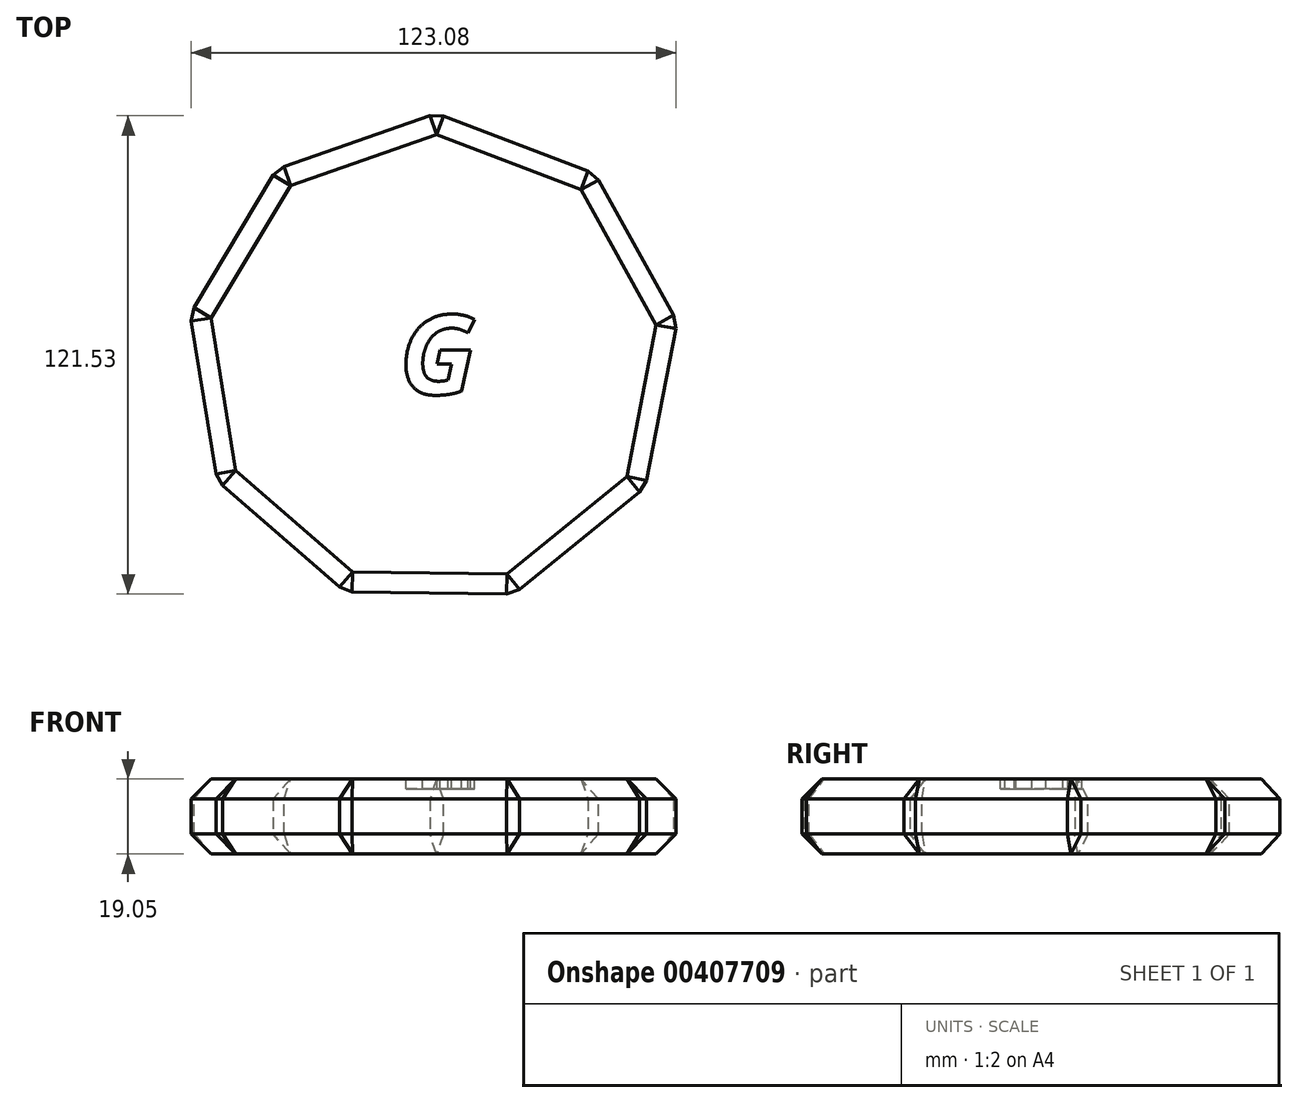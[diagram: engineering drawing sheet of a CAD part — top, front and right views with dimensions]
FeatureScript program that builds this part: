
annotation { "Feature Type Name" : "Feature", "Feature Type Description" : "" }
export const myFeature = defineFeature(function(context is Context, id is Id, definition is map)
    precondition{}
    {
        {
            var Q0;
            Q0=qCreatedBy(makeId("Top.planeOp"),FACE);
            var sketch = newSketch(context, id + "F0", { "sketchPlane" : qUnion([Q0])});
            skCircle(sketch, "E0.cCircle", {"center": v(3.24, 5.3) * mm, "radius": 59.03 * mm, "construction": true});
            skLineSegment(sketch, "E0.0", {"start": v(44.35, 52.8) * mm, "end": v(65.26, 15.27) * mm});
            skLineSegment(sketch, "E0.1", {"start": v(65.26, 15.27) * mm, "end": v(57.16, -26.93) * mm});
            skLineSegment(sketch, "E0.2", {"start": v(57.16, -26.93) * mm, "end": v(23.82, -54.05) * mm});
            skLineSegment(sketch, "E0.3", {"start": v(23.82, -54.05) * mm, "end": v(-19.14, -53.4) * mm});
            skLineSegment(sketch, "E0.4", {"start": v(-19.14, -53.4) * mm, "end": v(-51.63, -25.27) * mm});
            skLineSegment(sketch, "E0.5", {"start": v(-51.63, -25.27) * mm, "end": v(-58.45, 17.16) * mm});
            skLineSegment(sketch, "E0.6", {"start": v(-58.45, 17.16) * mm, "end": v(-36.4, 54.04) * mm});
            skLineSegment(sketch, "E0.7", {"start": v(-36.4, 54.04) * mm, "end": v(4.2, 68.11) * mm});
            skLineSegment(sketch, "E0.8", {"start": v(4.2, 68.11) * mm, "end": v(44.35, 52.8) * mm});
            skPoint(sketch, "E0.0.midPoint", {"position": v(54.8, 34.03) * mm});
            skSolve(sketch);
        }
        {
            var Q0;
            Q0=makeQuery(id+"F0.imprint","IMPRINT",FACE,{"disambiguationData":[TD([[makeQuery(id+"F0.imprint","IMPRINT",EDGE,{"derivedFrom":sQuery(id+"F0.wireOp",EDGE,"E0.0")}),-1.0]])]});
            extrude(context, id + "F1", {"entities" : qUnion([Q0]), "depth" : 19.05 * mm});
        }
        {
            var Q0;
            Q0=makeQuery(id+"F1.opExtrude","CAP_FACE",FACE,{"disambiguationData":[OSD([sQuery(id+"F0.wireOp",EDGE,"E0.0"),sQuery(id+"F0.wireOp",EDGE,"E0.1"),sQuery(id+"F0.wireOp",EDGE,"E0.2"),sQuery(id+"F0.wireOp",EDGE,"E0.3"),sQuery(id+"F0.wireOp",EDGE,"E0.4"),sQuery(id+"F0.wireOp",EDGE,"E0.5"),sQuery(id+"F0.wireOp",EDGE,"E0.6"),sQuery(id+"F0.wireOp",EDGE,"E0.7"),sQuery(id+"F0.wireOp",EDGE,"E0.8")])],"isStart":false});
            var sketch = newSketch(context, id + "F2", { "sketchPlane" : qUnion([Q0])});
            skText(sketch, "E1", { "text": "G", "fontName": "OpenSans-BoldItalic.ttf"});
            const initialGuessF2  = {"E1": [-0.00532, -0.00325, 1, 0, 0.02026]};
            skSetInitialGuess(sketch, initialGuessF2);
            skSolve(sketch);
        }
        {
            var Q0;
            Q0=makeQuery(id+"F1.opExtrude","CAP_FACE",FACE,{"disambiguationData":[OSD([sQuery(id+"F0.wireOp",EDGE,"E0.0"),sQuery(id+"F0.wireOp",EDGE,"E0.1"),sQuery(id+"F0.wireOp",EDGE,"E0.2"),sQuery(id+"F0.wireOp",EDGE,"E0.3"),sQuery(id+"F0.wireOp",EDGE,"E0.4"),sQuery(id+"F0.wireOp",EDGE,"E0.5"),sQuery(id+"F0.wireOp",EDGE,"E0.6"),sQuery(id+"F0.wireOp",EDGE,"E0.7"),sQuery(id+"F0.wireOp",EDGE,"E0.8")])],"isStart":false});
            var Q1;
            Q1=makeQuery(id+"F1.opExtrude","SWEPT_FACE",FACE,{"disambiguationData":[OSD([sQuery(id+"F0.wireOp",EDGE,"E0.3")])]});
            var Q2;
            Q2=makeQuery(id+"F1.opExtrude","SWEPT_FACE",FACE,{"disambiguationData":[OSD([sQuery(id+"F0.wireOp",EDGE,"E0.4")])]});
            var Q3;
            Q3=makeQuery(id+"F1.opExtrude","SWEPT_FACE",FACE,{"disambiguationData":[OSD([sQuery(id+"F0.wireOp",EDGE,"E0.5")])]});
            var Q4;
            Q4=makeQuery(id+"F1.opExtrude","SWEPT_FACE",FACE,{"disambiguationData":[OSD([sQuery(id+"F0.wireOp",EDGE,"E0.6")])]});
            var Q5;
            Q5=makeQuery(id+"F1.opExtrude","SWEPT_FACE",FACE,{"disambiguationData":[OSD([sQuery(id+"F0.wireOp",EDGE,"E0.8")])]});
            var Q6;
            Q6=makeQuery(id+"F1.opExtrude","SWEPT_FACE",FACE,{"disambiguationData":[OSD([sQuery(id+"F0.wireOp",EDGE,"E0.7")])]});
            var Q7;
            Q7=makeQuery(id+"F1.opExtrude","SWEPT_FACE",FACE,{"disambiguationData":[OSD([sQuery(id+"F0.wireOp",EDGE,"E0.0")])]});
            var Q8;
            Q8=makeQuery(id+"F1.opExtrude","SWEPT_FACE",FACE,{"disambiguationData":[OSD([sQuery(id+"F0.wireOp",EDGE,"E0.1")])]});
            var Q9;
            Q9=makeQuery(id+"F1.opExtrude","SWEPT_FACE",FACE,{"disambiguationData":[OSD([sQuery(id+"F0.wireOp",EDGE,"E0.2")])]});
            chamfer(context, id + "F3", {"entities" : qUnion([Q0, Q1, Q2, Q3, Q4, Q5, Q6, Q7, Q8, Q9]), "width" : 5.08 * mm, "tangentPropagation" : true});
        }
        {
            var Q0;
            Q0=makeQuery(id+"F2.imprint","IMPRINT",FACE,{"disambiguationData":[TD([[makeQuery(id+"F2.imprint","IMPRINT",EDGE,{"derivedFrom":sQuery(id+"F2.wireOp",EDGE,"E1.sketch_text.stroke-0")}),-1.0]])]});
            extrude(context, id + "F4", {"entities" : qUnion([Q0]), "operationType" : NewBodyOperationType.REMOVE, "oppositeDirection" : true, "depth" : 2.54 * mm});
        }
    });
